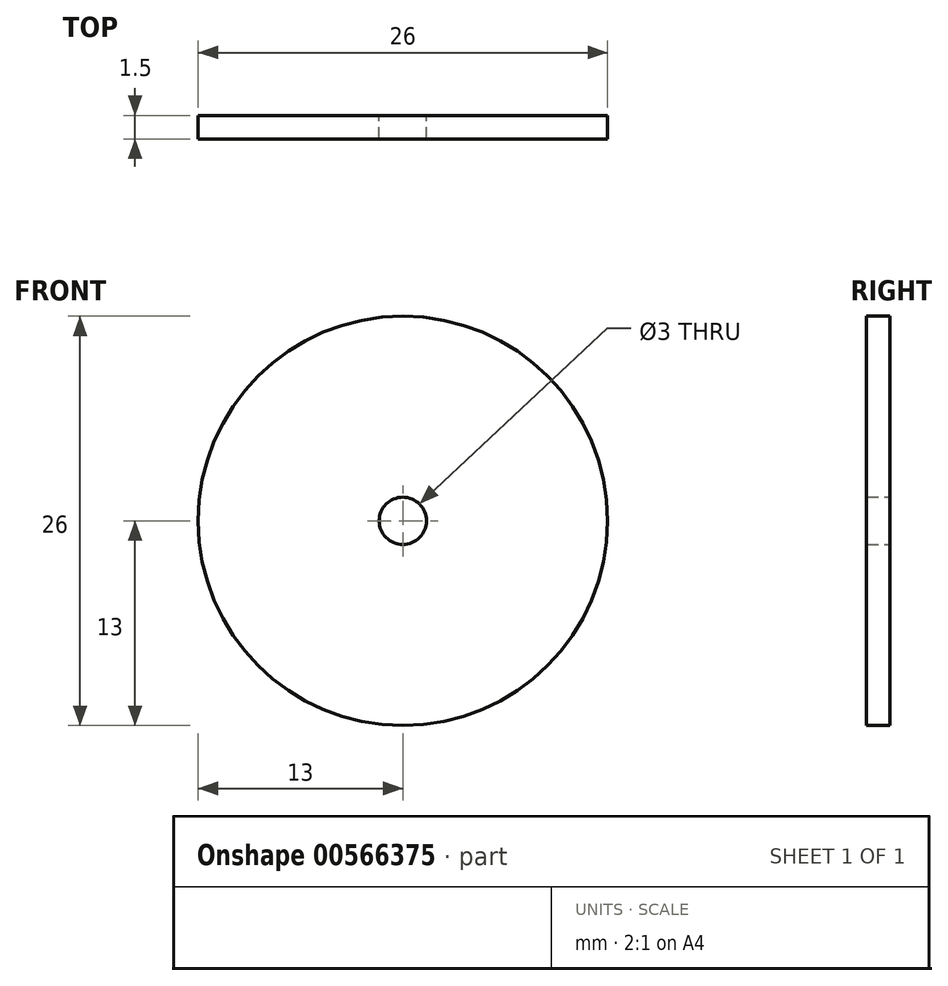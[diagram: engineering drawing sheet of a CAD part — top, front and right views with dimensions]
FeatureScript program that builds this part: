
annotation { "Feature Type Name" : "Feature", "Feature Type Description" : "" }
export const myFeature = defineFeature(function(context is Context, id is Id, definition is map)
    precondition{}
    {
        {
            var Q0;
            Q0=qCreatedBy(makeId("Front.planeOp"),FACE);
            var sketch = newSketch(context, id + "F0", { "sketchPlane" : qUnion([Q0])});
            skCircle(sketch, "E0", {"center": v(0, 0) * mm, "radius": 13 * mm});
            skCircle(sketch, "E1", {"center": v(0, 0) * mm, "radius": 1.5 * mm});
            skSolve(sketch);
        }
        {
            var Q0;
            Q0=makeQuery(id+"F0.imprint","IMPRINT",FACE,{"disambiguationData":[TD([[makeQuery(id+"F0.imprint","IMPRINT",EDGE,{"derivedFrom":sQuery(id+"F0.wireOp",EDGE,"E0")}),1.0]])]});
            extrude(context, id + "F1", {"entities" : qUnion([Q0]), "depth" : 1.5 * mm, "offsetDistance" : 25 * mm});
        }
    });
